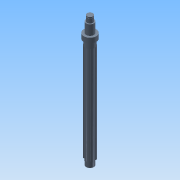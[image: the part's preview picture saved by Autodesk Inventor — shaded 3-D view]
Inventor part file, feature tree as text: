
AUTODESK INVENTOR PART (.ipt)
format: ipt  version: 2015 (Build 190159000, 159)  size: 169,472 bytes
history: native  units: mm
features: sketch x8, extrude x7, chamfer x1, pattern_circular x1, revolve x1, plane x1
ambient origin geometry x8: Origin, YZ Plane, XZ Plane, XY Plane, X Axis, Y Axis, Z Axis, Center Point
bodies: 实体1 (feature_tree)
feature tree (19):
  extrude  "拉伸1"  Depth=25.0mm TaperAngle=0.0deg
  extrude  "拉伸2"  Depth=80.0mm TaperAngle=0.0deg
  extrude  "拉伸3"  Depth=535.0mm TaperAngle=0.0deg
  extrude  "拉伸4"  Depth=30.0mm TaperAngle=0.0deg
  chamfer  "倒角1"  Distance=2.0mm Angle=45.0deg
  extrude  "拉伸5"  Depth=40.0mm
  pattern_circular  "环形阵列1"  Count=6 Angle=360.0deg
  extrude  "拉伸6"  Depth=10.0mm TaperAngle=0.0deg
  revolve  "旋转1"  Angle=360.0deg
  plane  "工作平面1"
  extrude  "拉伸7"  Depth=10.0mm
  sketch  "草图1"  dims[d0=64.0mm d1=25.0mm d2=0.0mm]
  sketch  "草图2"  dims[d3=40.0mm d4=80.0mm d5=0.0mm]
  sketch  "草图3"  dims[d6=50.0mm d7=535.0mm d8=0.0mm]
  sketch  "草图4"  dims[d9=40.0mm d10=30.0mm d11=0.0mm d12=2.0mm d13=2.0mm d14=45.0deg]
  sketch  "草图5"  dims[d15=50.0mm d16=40.0mm]
  sketch  "草图6"  dims[d17=7.253074mm]
  sketch  "草图7"  dims[d18=4.0mm]
  sketch  "草图8"  dims[d19=8.0mm d20=60.0mm d22=360.0deg d24=505.0mm d25=0.0mm d26=60.0mm d27=360.0deg d29=30.0mm d30=40.0mm d31=28.578mm d32=0.0mm d33=169.800173mm d34=13.95mm d35=4.248mm d36=1.4mm d37=5.0mm d38=90.0deg d39=8.0mm d40=10.0mm d41=6.589mm d42=18.230413mm d43=3.0mm d44=0.0mm]
